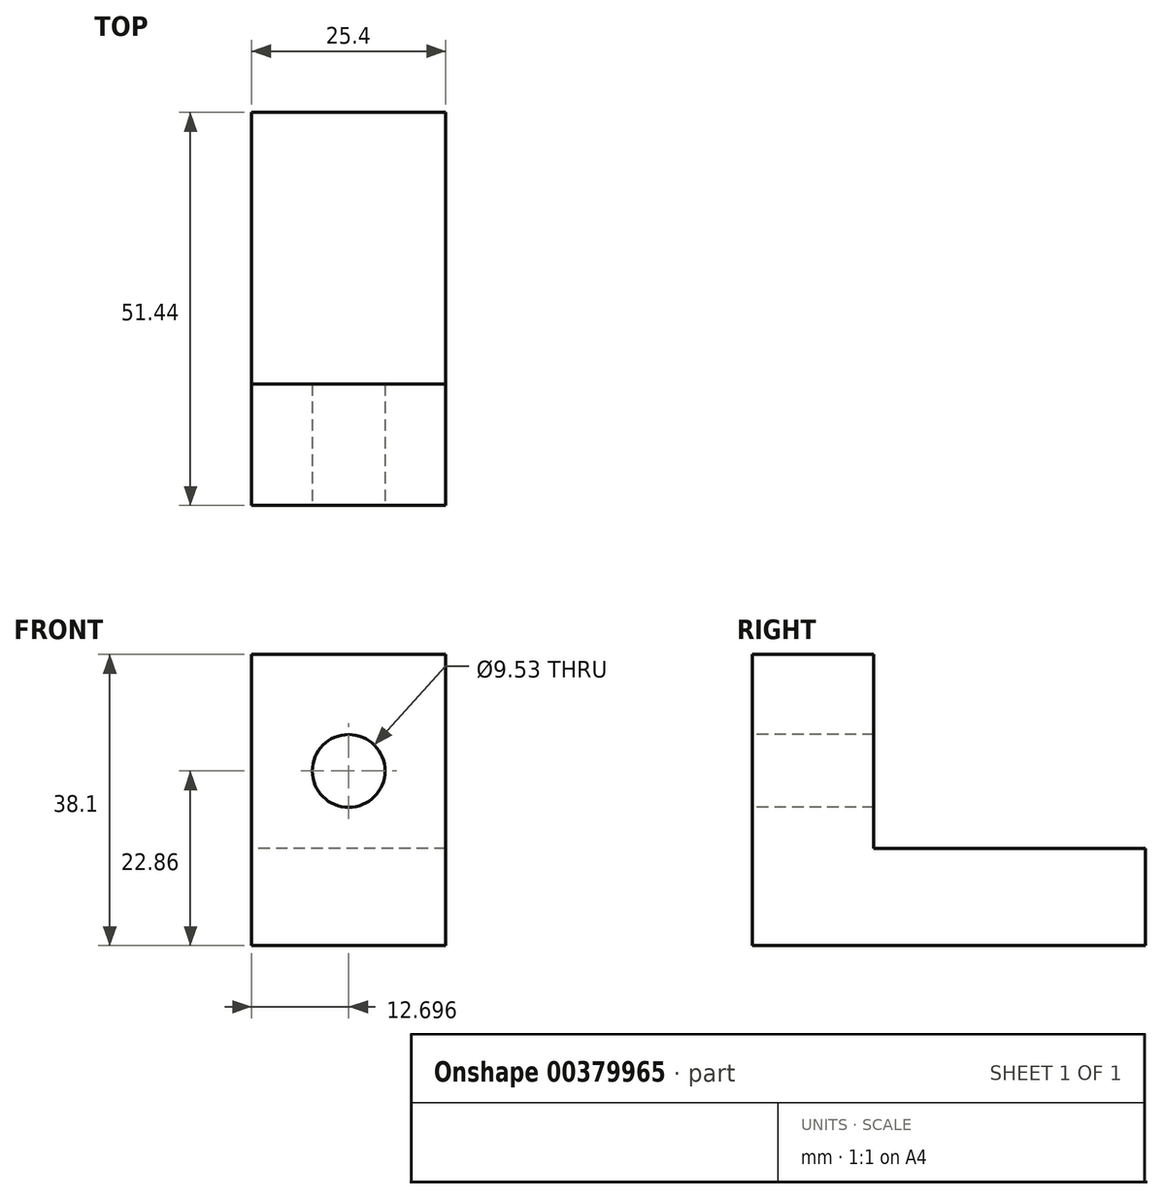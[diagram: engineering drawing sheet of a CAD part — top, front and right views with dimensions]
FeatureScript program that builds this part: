
annotation { "Feature Type Name" : "Feature", "Feature Type Description" : "" }
export const myFeature = defineFeature(function(context is Context, id is Id, definition is map)
    precondition{}
    {
        {
            var Q0;
            Q0=qCreatedBy(makeId("Top.planeOp"),FACE);
            var sketch = newSketch(context, id + "F0", { "sketchPlane" : qUnion([Q0])});
            skLineSegment(sketch, "E0.bottom", {"start": v(-57.97, -3.66) * mm, "end": v(-32.57, -3.66) * mm});
            skLineSegment(sketch, "E0.top", {"start": v(-57.97, -19.54) * mm, "end": v(-32.57, -19.54) * mm});
            skLineSegment(sketch, "E0.left", {"start": v(-57.97, -3.66) * mm, "end": v(-57.97, -19.54) * mm});
            skLineSegment(sketch, "E0.right", {"start": v(-32.57, -3.66) * mm, "end": v(-32.57, -19.54) * mm});
            skSolve(sketch);
        }
        {
            var Q0;
            Q0 = qSketchRegion(id + "F0", true);
            extrude(context, id + "F1", {"entities" : qUnion([Q0]), "depth" : 38.1 * mm});
        }
        {
            var Q0;
            Q0=makeQuery(id+"F1.opExtrude","SWEPT_FACE",FACE,{"disambiguationData":[OSD([sQuery(id+"F0.wireOp",EDGE,"E0.top")])]});
            var sketch = newSketch(context, id + "F2", { "sketchPlane" : qUnion([Q0])});
            skCircle(sketch, "E1", {"center": v(-45.27, 22.86) * mm, "radius": 4.76 * mm});
            skSolve(sketch);
        }
        {
            var Q0;
            Q0 = qSketchRegion(id + "F2", true);
            extrude(context, id + "F3", {"entities" : qUnion([Q0]), "operationType" : NewBodyOperationType.REMOVE, "oppositeDirection" : true, "depth" : 254000 * mm});
        }
        {
            var Q0;
            Q0=makeQuery(id+"F1.opExtrude","SWEPT_FACE",FACE,{"disambiguationData":[OSD([sQuery(id+"F0.wireOp",EDGE,"E0.bottom")])]});
            var sketch = newSketch(context, id + "F4", { "sketchPlane" : qUnion([Q0])});
            skLineSegment(sketch, "E2.bottom", {"start": v(32.57, 12.7) * mm, "end": v(57.97, 12.7) * mm});
            skLineSegment(sketch, "E2.top", {"start": v(32.57, 0) * mm, "end": v(57.97, 0) * mm});
            skLineSegment(sketch, "E2.left", {"start": v(32.57, 12.7) * mm, "end": v(32.57, 0) * mm});
            skLineSegment(sketch, "E2.right", {"start": v(57.97, 12.7) * mm, "end": v(57.97, 0) * mm});
            skSolve(sketch);
        }
        {
            var Q0;
            Q0 = qSketchRegion(id + "F4", true);
            extrude(context, id + "F5", {"entities" : qUnion([Q0]), "operationType" : NewBodyOperationType.ADD, "depth" : 35.56 * mm});
        }
    });
